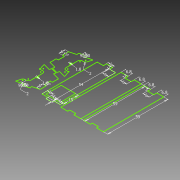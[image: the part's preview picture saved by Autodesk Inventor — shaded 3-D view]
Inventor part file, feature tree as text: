
AUTODESK INVENTOR PART (.ipt)
format: ipt  version: 2012 (Build 160160000, 160)  size: 112,640 bytes
history: native  units: mm
features: sketch x1
ambient origin geometry x8: Origin, YZ Plane, XZ Plane, XY Plane, X Axis, Y Axis, Z Axis, Center Point
feature tree (1):
  sketch  "Sketch1"  dims[d423=2.0mm d475=1.8mm d480=2.0mm d481=6.0mm d483=3.0mm d484=2.0mm d485=90.0deg d493=6.0mm d494=2.0mm d496=6.0mm d497=6.0mm d506=54.0mm d508=6.0mm d509=3.0mm d510=6.0mm d512=6.8mm d513=6.0mm d514=6.8mm d515=59.0mm d516=6.8mm d517=6.0mm d518=6.8mm d519=59.0mm d520=15.0mm d521=3.0mm d522=3.0mm d526=2.0mm d527=1.8mm d528=2.0mm d529=6.0mm d530=3.0mm d531=2.0mm d532=90.0deg]
